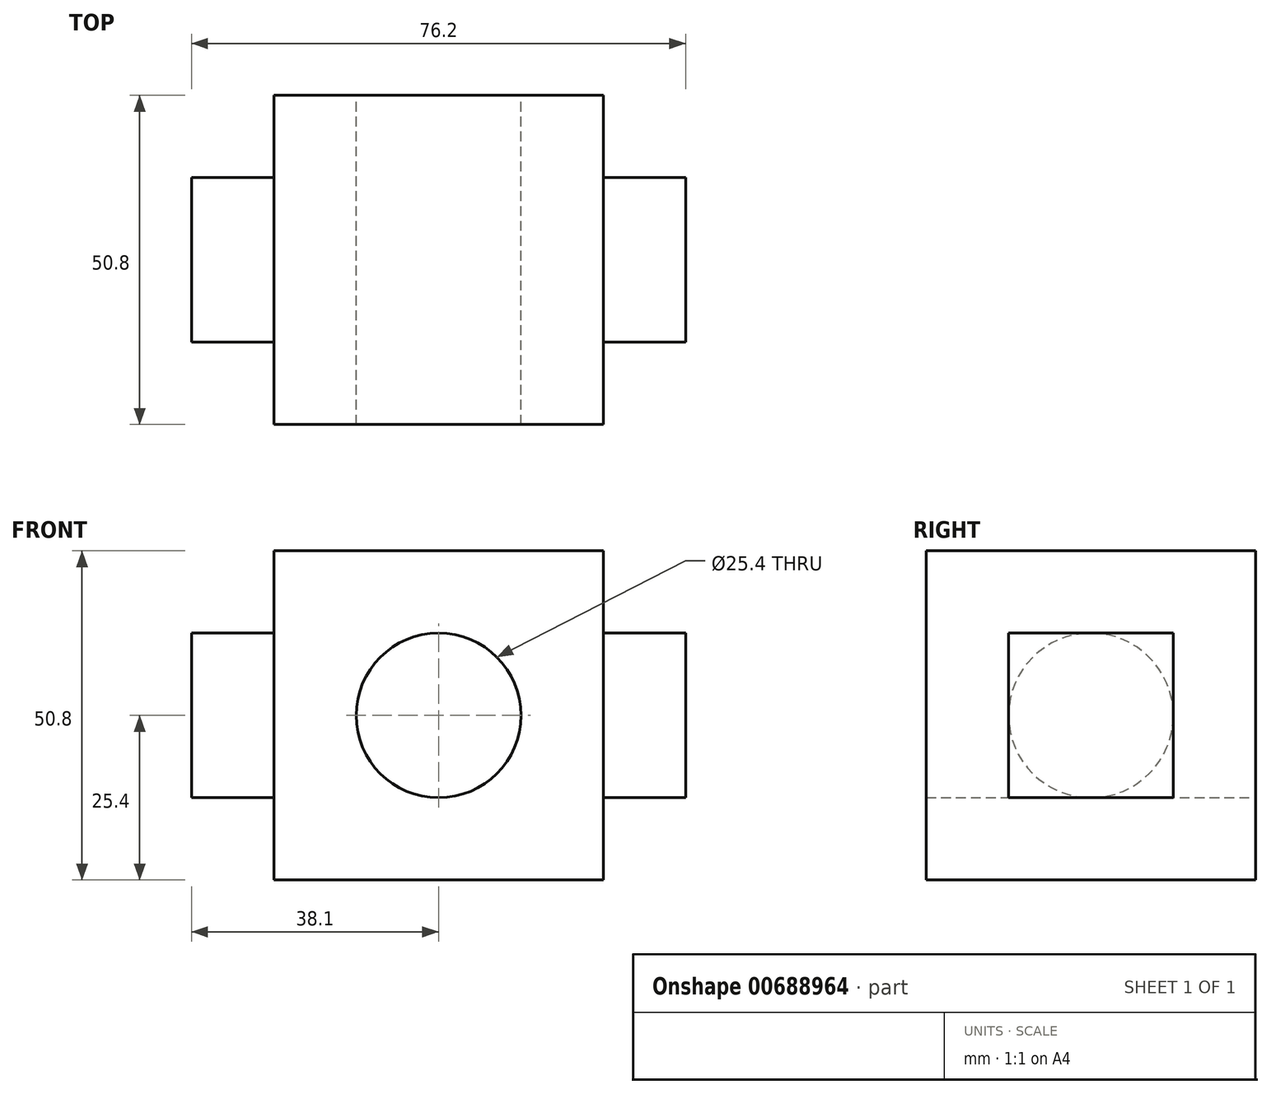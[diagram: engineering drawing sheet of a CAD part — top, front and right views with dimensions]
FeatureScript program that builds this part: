
annotation { "Feature Type Name" : "Feature", "Feature Type Description" : "" }
export const myFeature = defineFeature(function(context is Context, id is Id, definition is map)
    precondition{}
    {
        {
            var Q0;
            Q0=qCreatedBy(makeId("Front.planeOp"),FACE);
            var sketch = newSketch(context, id + "F0", { "sketchPlane" : qUnion([Q0])});
            skLineSegment(sketch, "E0.bottom", {"start": v(0, 0) * mm, "end": v(50.8, 0) * mm});
            skLineSegment(sketch, "E0.top", {"start": v(0, 50.8) * mm, "end": v(50.8, 50.8) * mm});
            skLineSegment(sketch, "E0.left", {"start": v(0, 0) * mm, "end": v(0, 50.8) * mm});
            skLineSegment(sketch, "E0.right", {"start": v(50.8, 0) * mm, "end": v(50.8, 50.8) * mm});
            skSolve(sketch);
        }
        {
            var Q0;
            Q0=makeQuery(id+"F0.imprint","IMPRINT",FACE,{"disambiguationData":[TD([[makeQuery(id+"F0.imprint","IMPRINT",EDGE,{"derivedFrom":sQuery(id+"F0.wireOp",EDGE,"E0.bottom")}),1.0]])]});
            var sketch = newSketch(context, id + "F1", { "sketchPlane" : qUnion([Q0])});
            skCircle(sketch, "E1", {"center": v(25.4, 25.4) * mm, "radius": 12.7 * mm});
            skSolve(sketch);
        }
        {
            var Q0;
            Q0=makeQuery(id+"F1.imprint","IMPRINT",FACE,{"disambiguationData":[TD([[makeQuery(id+"F1.imprint","IMPRINT",EDGE,{"derivedFrom":sQuery(id+"F1.wireOp",EDGE,"E1")}),-1.0]])]});
            extrude(context, id + "F2", {"entities" : qUnion([Q0]), "depth" : 50.8 * mm, "offsetDistance" : 25.4 * mm});
        }
        {
            var Q0;
            Q0=makeQuery(id+"F2.opExtrude","SWEPT_FACE",FACE,{"disambiguationData":[OSD([sQuery(id+"F0.wireOp",EDGE,"E0.right")])]});
            var sketch = newSketch(context, id + "F3", { "sketchPlane" : qUnion([Q0])});
            skLineSegment(sketch, "E2.bottom", {"start": v(-12.7, 38.1) * mm, "end": v(-38.1, 38.1) * mm});
            skLineSegment(sketch, "E2.top", {"start": v(-12.7, 12.7) * mm, "end": v(-38.1, 12.7) * mm});
            skLineSegment(sketch, "E2.left", {"start": v(-12.7, 38.1) * mm, "end": v(-12.7, 12.7) * mm});
            skLineSegment(sketch, "E2.right", {"start": v(-38.1, 38.1) * mm, "end": v(-38.1, 12.7) * mm});
            skPoint(sketch, "E2.middle", {"position": v(-25.4, 25.4) * mm});
            skSolve(sketch);
        }
        {
            var Q0;
            Q0=makeQuery(id+"F3.imprint","IMPRINT",FACE,{"disambiguationData":[TD([[makeQuery(id+"F3.imprint","IMPRINT",EDGE,{"derivedFrom":sQuery(id+"F3.wireOp",EDGE,"E2.bottom")}),1.0]])]});
            extrude(context, id + "F4", {"entities" : qUnion([Q0]), "operationType" : NewBodyOperationType.ADD, "depth" : 12.7 * mm, "offsetDistance" : 25.4 * mm});
        }
        {
            var Q0;
            Q0=makeQuery(id+"F2.opExtrude","SWEPT_FACE",FACE,{"disambiguationData":[OSD([sQuery(id+"F0.wireOp",EDGE,"E0.left")])]});
            var sketch = newSketch(context, id + "F5", { "sketchPlane" : qUnion([Q0])});
            skCircle(sketch, "E3", {"center": v(25.4, 25.4) * mm, "radius": 12.7 * mm});
            skSolve(sketch);
        }
        {
            var Q0;
            Q0=makeQuery(id+"F5.imprint","IMPRINT",FACE,{"disambiguationData":[TD([[makeQuery(id+"F5.imprint","IMPRINT",EDGE,{"derivedFrom":sQuery(id+"F5.wireOp",EDGE,"E3")}),1.0]])]});
            extrude(context, id + "F6", {"entities" : qUnion([Q0]), "operationType" : NewBodyOperationType.ADD, "depth" : 12.7 * mm, "offsetDistance" : 25.4 * mm});
        }
    });
